# Revit family: Bathtub
name_source: partatom
category: Plumbing Fixtures
units: mm (PartAtom-declared; Revit-internal decimal feet)

## family parameters
Always vertical = Yes
Classification Number = 23.45.05.14.21
Cut with Voids When Loaded = No
Enable Cutting in Views = No
Maintain Annotation Orientation = No
Part Type = Normal
Room Calculation Point = No
Round Connector Dimension = Use Diameter
Shared = Yes
Work Plane-Based = Yes

## types (1)
- Bathtub
    Assembly Code = D2010510
    CW Connection = Yes
    Construction Details = http://www.arcat.com
    Control Height = 2' - 6"
    Default Elevation = 4' - 0"
    Description = Bathtub
    Expected Lifespan (Years) = 20
    Finish - Bath Fittings = ARCAT - Enamel Coating - Azure
    Finish - Bath Fixtures = ARCAT - Metal - Brass
    Green Building - LEED = http://www.arcat.com
    HW Connection = Yes
    Keynote = 15410
    Length = 5' - 0"
    Maintenance Schedule (Months) = 12
    Manufacturer = Generic
    Manufacturer Fax = (203) 939-2444
    Manufacturer Website = http://www.arcat.com
    Material - Bath Fittings = ARCAT - Fiberglass
    Model = Generic
    Perimeter = 0' - 4"
    Product Data = http://www.arcat.com
    Product Properties = http://www.arcat.com
    Rad A = 0' - 11 15/32"
    Specification = http://www.arcat.com
    Tub Depth = 1' - 6"
    Tub Spout Height = 1' - 9"
    Vent Connection = No
    Warranty Duration (Years) = 10
    Waste Connection = Yes
    Width = 2' - 6"

## geometry (parser evidence)
native form markers: Sweep x8
no freeform markers — native parametric forms only
